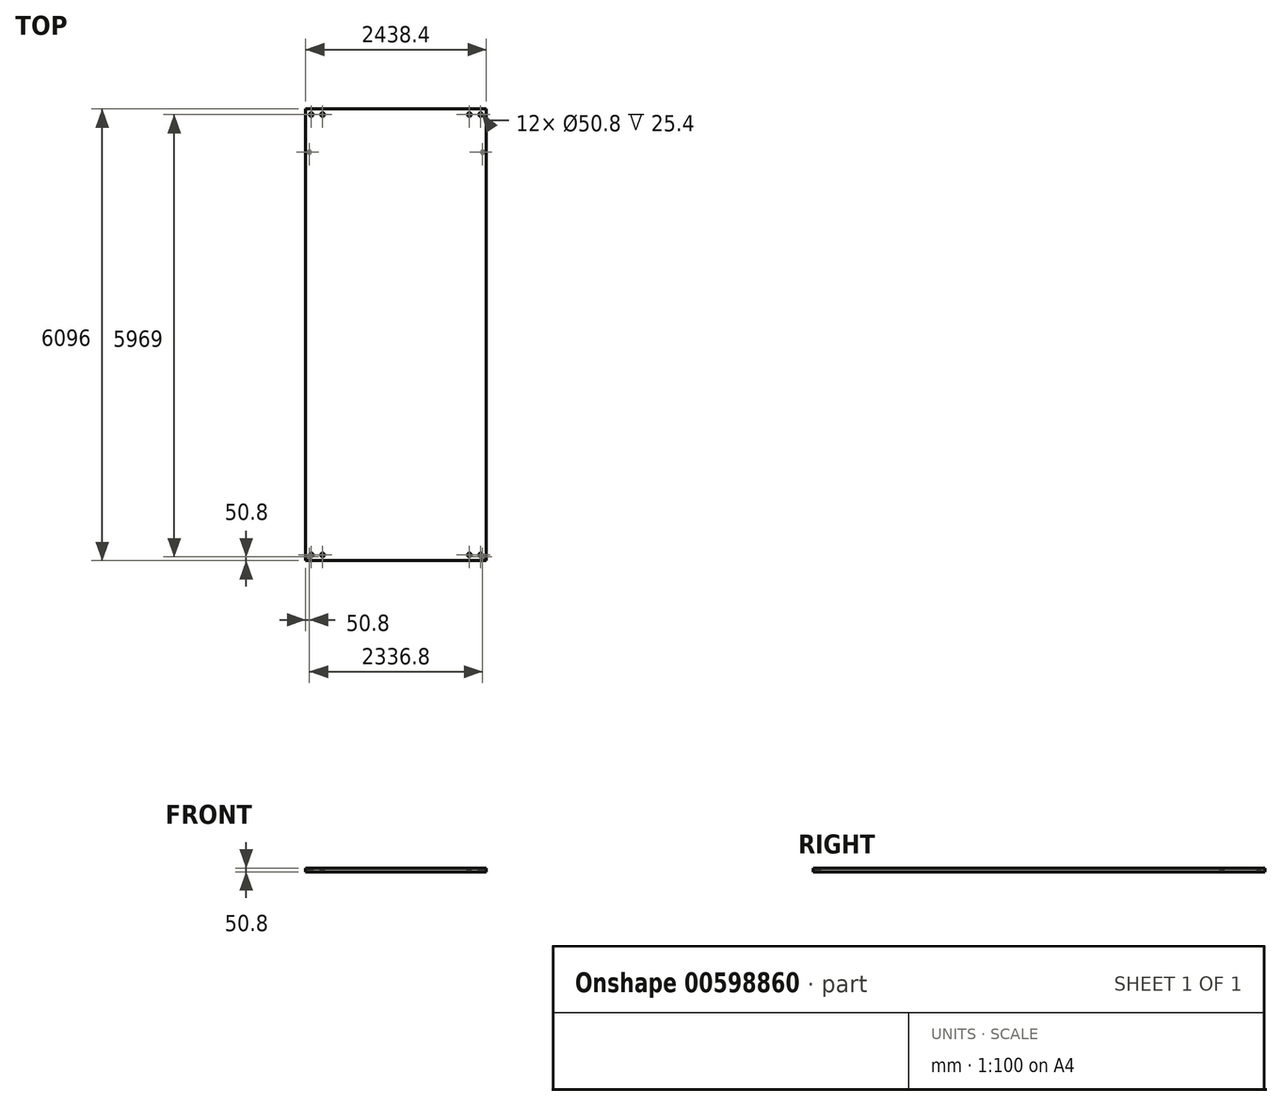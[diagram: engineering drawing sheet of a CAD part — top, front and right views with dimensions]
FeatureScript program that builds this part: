
annotation { "Feature Type Name" : "Feature", "Feature Type Description" : "" }
export const myFeature = defineFeature(function(context is Context, id is Id, definition is map)
    precondition{}
    {
        {
            var Q0;
            Q0=qCreatedBy(makeId("Top.planeOp"),FACE);
            var sketch = newSketch(context, id + "F0", { "sketchPlane" : qUnion([Q0])});
            skLineSegment(sketch, "E0.bottom", {"start": v(1219.2, 3048) * mm, "end": v(-1219.2, 3048) * mm});
            skLineSegment(sketch, "E0.top", {"start": v(1219.2, -3048) * mm, "end": v(-1219.2, -3048) * mm});
            skLineSegment(sketch, "E0.left", {"start": v(1219.2, 3048) * mm, "end": v(1219.2, -3048) * mm});
            skLineSegment(sketch, "E0.right", {"start": v(-1219.2, 3048) * mm, "end": v(-1219.2, -3048) * mm});
            skPoint(sketch, "E0.middle", {"position": v(0, 0) * mm});
            skSolve(sketch);
        }
        {
            var Q0;
            Q0=makeQuery(id+"F0.imprint","IMPRINT",FACE,{"disambiguationData":[TD([[makeQuery(id+"F0.imprint","IMPRINT",EDGE,{"derivedFrom":sQuery(id+"F0.wireOp",EDGE,"E0.bottom")}),1.0]])]});
            extrude(context, id + "F1", {"entities" : qUnion([Q0]), "depth" : 50.8 * mm, "offsetDistance" : 25.4 * mm});
        }
        {
            var Q0;
            Q0=makeQuery(id+"F1.opExtrude","CAP_FACE",FACE,{"disambiguationData":[OSD([sQuery(id+"F0.wireOp",EDGE,"E0.bottom"),sQuery(id+"F0.wireOp",EDGE,"E0.top"),sQuery(id+"F0.wireOp",EDGE,"E0.left"),sQuery(id+"F0.wireOp",EDGE,"E0.right")])],"isStart":false});
            var sketch = newSketch(context, id + "F2", { "sketchPlane" : qUnion([Q0])});
            skLineSegment(sketch, "E1.bottom", {"start": v(1219.2, -3048) * mm, "end": v(1143, -3048) * mm});
            skLineSegment(sketch, "E1.top", {"start": v(1219.2, -2971.8) * mm, "end": v(1143, -2971.8) * mm});
            skLineSegment(sketch, "E1.left", {"start": v(1219.2, -3048) * mm, "end": v(1219.2, -2971.8) * mm});
            skLineSegment(sketch, "E1.right", {"start": v(1143, -3048) * mm, "end": v(1143, -2971.8) * mm});
            skLineSegment(sketch, "E2.bottom", {"start": v(-1219.2, -3048) * mm, "end": v(-1143, -3048) * mm});
            skLineSegment(sketch, "E2.top", {"start": v(-1219.2, -2971.8) * mm, "end": v(-1143, -2971.8) * mm});
            skLineSegment(sketch, "E2.left", {"start": v(-1219.2, -3048) * mm, "end": v(-1219.2, -2971.8) * mm});
            skLineSegment(sketch, "E2.right", {"start": v(-1143, -3048) * mm, "end": v(-1143, -2971.8) * mm});
            skLineSegment(sketch, "E3.bottom", {"start": v(1219.2, 3048) * mm, "end": v(1143, 3048) * mm});
            skLineSegment(sketch, "E3.top", {"start": v(1219.2, 2971.8) * mm, "end": v(1143, 2971.8) * mm});
            skLineSegment(sketch, "E3.left", {"start": v(1219.2, 3048) * mm, "end": v(1219.2, 2971.8) * mm});
            skLineSegment(sketch, "E3.right", {"start": v(1143, 3048) * mm, "end": v(1143, 2971.8) * mm});
            skLineSegment(sketch, "E4.bottom", {"start": v(-1219.2, 3048) * mm, "end": v(-1143, 3048) * mm});
            skLineSegment(sketch, "E4.top", {"start": v(-1219.2, 2971.8) * mm, "end": v(-1143, 2971.8) * mm});
            skLineSegment(sketch, "E4.left", {"start": v(-1219.2, 3048) * mm, "end": v(-1219.2, 2971.8) * mm});
            skLineSegment(sketch, "E4.right", {"start": v(-1143, 3048) * mm, "end": v(-1143, 2971.8) * mm});
            skCircle(sketch, "E5", {"center": v(-1143, 2971.8) * mm, "radius": 25.4 * mm});
            skCircle(sketch, "E6", {"center": v(1143, 2971.8) * mm, "radius": 25.4 * mm});
            skCircle(sketch, "E7", {"center": v(1143, -2971.8) * mm, "radius": 25.4 * mm});
            skCircle(sketch, "E8", {"center": v(-1143, -2971.8) * mm, "radius": 25.4 * mm});
            skSolve(sketch);
        }
        {
            var Q0;
            {var subQ0=sQuery(id+"F2.wireOp",EDGE,"E3.right");var subQ1=sQuery(id+"F2.wireOp",EDGE,"E3.top");var subQ2=makeQuery(id+"F2.imprint","INTERSECT",VERTEX,{"derivedFrom":[subQ1,subQ0]});Q0=makeQuery(id+"F2.imprint","IMPRINT",FACE,{"disambiguationData":[TD([[makeQuery(id+"F2.imprint","IMPRINT",EDGE,{"disambiguationData":[TD([[subQ2,1.0]])],"derivedFrom":subQ1}),-1.0]])]});}
            var Q1;
            {var subQ0=sQuery(id+"F2.wireOp",EDGE,"E3.right");var subQ1=sQuery(id+"F2.wireOp",EDGE,"E3.top");var subQ2=makeQuery(id+"F2.imprint","INTERSECT",VERTEX,{"derivedFrom":[subQ1,subQ0]});Q1=makeQuery(id+"F2.imprint","IMPRINT",FACE,{"disambiguationData":[TD([[makeQuery(id+"F2.imprint","IMPRINT",EDGE,{"disambiguationData":[TD([[subQ2,1.0]])],"derivedFrom":subQ1}),1.0]])]});}
            var Q2;
            {var subQ0=sQuery(id+"F2.wireOp",EDGE,"E1.right");var subQ1=sQuery(id+"F2.wireOp",EDGE,"E1.top");var subQ2=makeQuery(id+"F2.imprint","INTERSECT",VERTEX,{"derivedFrom":[subQ1,subQ0]});Q2=makeQuery(id+"F2.imprint","IMPRINT",FACE,{"disambiguationData":[TD([[makeQuery(id+"F2.imprint","IMPRINT",EDGE,{"disambiguationData":[TD([[subQ2,1.0]])],"derivedFrom":subQ1}),1.0]])]});}
            var Q3;
            {var subQ0=sQuery(id+"F2.wireOp",EDGE,"E1.right");var subQ1=sQuery(id+"F2.wireOp",EDGE,"E1.top");var subQ2=makeQuery(id+"F2.imprint","INTERSECT",VERTEX,{"derivedFrom":[subQ1,subQ0]});Q3=makeQuery(id+"F2.imprint","IMPRINT",FACE,{"disambiguationData":[TD([[makeQuery(id+"F2.imprint","IMPRINT",EDGE,{"disambiguationData":[TD([[subQ2,1.0]])],"derivedFrom":subQ1}),-1.0]])]});}
            var Q4;
            {var subQ0=sQuery(id+"F2.wireOp",EDGE,"E2.right");var subQ1=sQuery(id+"F2.wireOp",EDGE,"E2.top");var subQ2=makeQuery(id+"F2.imprint","INTERSECT",VERTEX,{"derivedFrom":[subQ1,subQ0]});Q4=makeQuery(id+"F2.imprint","IMPRINT",FACE,{"disambiguationData":[TD([[makeQuery(id+"F2.imprint","IMPRINT",EDGE,{"disambiguationData":[TD([[subQ2,1.0]])],"derivedFrom":subQ1}),-1.0]])]});}
            var Q5;
            {var subQ0=sQuery(id+"F2.wireOp",EDGE,"E2.right");var subQ1=sQuery(id+"F2.wireOp",EDGE,"E2.top");var subQ2=makeQuery(id+"F2.imprint","INTERSECT",VERTEX,{"derivedFrom":[subQ1,subQ0]});Q5=makeQuery(id+"F2.imprint","IMPRINT",FACE,{"disambiguationData":[TD([[makeQuery(id+"F2.imprint","IMPRINT",EDGE,{"disambiguationData":[TD([[subQ2,1.0]])],"derivedFrom":subQ1}),1.0]])]});}
            var Q6;
            {var subQ0=sQuery(id+"F2.wireOp",EDGE,"E4.right");var subQ1=sQuery(id+"F2.wireOp",EDGE,"E4.top");var subQ2=makeQuery(id+"F2.imprint","INTERSECT",VERTEX,{"derivedFrom":[subQ1,subQ0]});Q6=makeQuery(id+"F2.imprint","IMPRINT",FACE,{"disambiguationData":[TD([[makeQuery(id+"F2.imprint","IMPRINT",EDGE,{"disambiguationData":[TD([[subQ2,1.0]])],"derivedFrom":subQ1}),1.0]])]});}
            var Q7;
            {var subQ0=sQuery(id+"F2.wireOp",EDGE,"E4.right");var subQ1=sQuery(id+"F2.wireOp",EDGE,"E4.top");var subQ2=makeQuery(id+"F2.imprint","INTERSECT",VERTEX,{"derivedFrom":[subQ1,subQ0]});Q7=makeQuery(id+"F2.imprint","IMPRINT",FACE,{"disambiguationData":[TD([[makeQuery(id+"F2.imprint","IMPRINT",EDGE,{"disambiguationData":[TD([[subQ2,1.0]])],"derivedFrom":subQ1}),-1.0]])]});}
            extrude(context, id + "F3", {"entities" : qUnion([Q0, Q1, Q2, Q3, Q4, Q5, Q6, Q7]), "operationType" : NewBodyOperationType.REMOVE, "oppositeDirection" : true, "depth" : 25.4 * mm, "offsetDistance" : 25.4 * mm});
        }
        {
            var Q0;
            Q0=makeQuery(id+"F1.opExtrude","CAP_FACE",FACE,{"disambiguationData":[OSD([sQuery(id+"F0.wireOp",EDGE,"E0.bottom"),sQuery(id+"F0.wireOp",EDGE,"E0.top"),sQuery(id+"F0.wireOp",EDGE,"E0.left"),sQuery(id+"F0.wireOp",EDGE,"E0.right")])],"isStart":false});
            var sketch = newSketch(context, id + "F4", { "sketchPlane" : qUnion([Q0])});
            skLineSegment(sketch, "E9.bottom", {"start": v(-1219.2, 3048) * mm, "end": v(-990.6, 3048) * mm});
            skLineSegment(sketch, "E9.top", {"start": v(-1219.2, 2971.8) * mm, "end": v(-990.6, 2971.8) * mm});
            skLineSegment(sketch, "E9.left", {"start": v(-1219.2, 3048) * mm, "end": v(-1219.2, 2971.8) * mm});
            skLineSegment(sketch, "E9.right", {"start": v(-990.6, 3048) * mm, "end": v(-990.6, 2971.8) * mm});
            skCircle(sketch, "E10", {"center": v(-990.6, 2971.8) * mm, "radius": 25.4 * mm});
            skLineSegment(sketch, "E11.bottom", {"start": v(1219.2, 3048) * mm, "end": v(990.6, 3048) * mm});
            skLineSegment(sketch, "E11.top", {"start": v(1219.2, 2971.8) * mm, "end": v(990.6, 2971.8) * mm});
            skLineSegment(sketch, "E11.left", {"start": v(1219.2, 3048) * mm, "end": v(1219.2, 2971.8) * mm});
            skLineSegment(sketch, "E11.right", {"start": v(990.6, 3048) * mm, "end": v(990.6, 2971.8) * mm});
            skCircle(sketch, "E12", {"center": v(990.6, 2971.8) * mm, "radius": 25.4 * mm});
            skLineSegment(sketch, "E13.bottom", {"start": v(-1219.2, -3048) * mm, "end": v(-990.6, -3048) * mm});
            skLineSegment(sketch, "E13.top", {"start": v(-1219.2, -2971.8) * mm, "end": v(-990.6, -2971.8) * mm});
            skLineSegment(sketch, "E13.left", {"start": v(-1219.2, -3048) * mm, "end": v(-1219.2, -2971.8) * mm});
            skLineSegment(sketch, "E13.right", {"start": v(-990.6, -3048) * mm, "end": v(-990.6, -2971.8) * mm});
            skLineSegment(sketch, "E14.bottom", {"start": v(1219.2, -3048) * mm, "end": v(990.6, -3048) * mm});
            skLineSegment(sketch, "E14.top", {"start": v(1219.2, -2971.8) * mm, "end": v(990.6, -2971.8) * mm});
            skLineSegment(sketch, "E14.left", {"start": v(1219.2, -3048) * mm, "end": v(1219.2, -2971.8) * mm});
            skLineSegment(sketch, "E14.right", {"start": v(990.6, -3048) * mm, "end": v(990.6, -2971.8) * mm});
            skCircle(sketch, "E15", {"center": v(-990.6, -2971.8) * mm, "radius": 25.4 * mm});
            skCircle(sketch, "E16", {"center": v(990.6, -2971.8) * mm, "radius": 25.4 * mm});
            skSolve(sketch);
        }
        {
            var Q0;
            {var subQ0=sQuery(id+"F4.wireOp",EDGE,"E14.right");var subQ1=sQuery(id+"F4.wireOp",EDGE,"E14.top");var subQ2=makeQuery(id+"F4.imprint","INTERSECT",VERTEX,{"derivedFrom":[subQ1,subQ0]});Q0=makeQuery(id+"F4.imprint","IMPRINT",FACE,{"disambiguationData":[TD([[makeQuery(id+"F4.imprint","IMPRINT",EDGE,{"disambiguationData":[TD([[subQ2,1.0]])],"derivedFrom":subQ1}),-1.0]])]});}
            var Q1;
            {var subQ0=sQuery(id+"F4.wireOp",EDGE,"E14.right");var subQ1=sQuery(id+"F4.wireOp",EDGE,"E14.top");var subQ2=makeQuery(id+"F4.imprint","INTERSECT",VERTEX,{"derivedFrom":[subQ1,subQ0]});Q1=makeQuery(id+"F4.imprint","IMPRINT",FACE,{"disambiguationData":[TD([[makeQuery(id+"F4.imprint","IMPRINT",EDGE,{"disambiguationData":[TD([[subQ2,1.0]])],"derivedFrom":subQ1}),1.0]])]});}
            var Q2;
            {var subQ0=sQuery(id+"F4.wireOp",EDGE,"E13.right");var subQ1=sQuery(id+"F4.wireOp",EDGE,"E13.top");var subQ2=makeQuery(id+"F4.imprint","INTERSECT",VERTEX,{"derivedFrom":[subQ1,subQ0]});Q2=makeQuery(id+"F4.imprint","IMPRINT",FACE,{"disambiguationData":[TD([[makeQuery(id+"F4.imprint","IMPRINT",EDGE,{"disambiguationData":[TD([[subQ2,1.0]])],"derivedFrom":subQ1}),-1.0]])]});}
            var Q3;
            {var subQ0=sQuery(id+"F4.wireOp",EDGE,"E13.right");var subQ1=sQuery(id+"F4.wireOp",EDGE,"E13.top");var subQ2=makeQuery(id+"F4.imprint","INTERSECT",VERTEX,{"derivedFrom":[subQ1,subQ0]});Q3=makeQuery(id+"F4.imprint","IMPRINT",FACE,{"disambiguationData":[TD([[makeQuery(id+"F4.imprint","IMPRINT",EDGE,{"disambiguationData":[TD([[subQ2,1.0]])],"derivedFrom":subQ1}),1.0]])]});}
            var Q4;
            {var subQ0=sQuery(id+"F4.wireOp",EDGE,"E11.right");var subQ1=sQuery(id+"F4.wireOp",EDGE,"E11.top");var subQ2=makeQuery(id+"F4.imprint","INTERSECT",VERTEX,{"derivedFrom":[subQ1,subQ0]});Q4=makeQuery(id+"F4.imprint","IMPRINT",FACE,{"disambiguationData":[TD([[makeQuery(id+"F4.imprint","IMPRINT",EDGE,{"disambiguationData":[TD([[subQ2,1.0]])],"derivedFrom":subQ1}),-1.0]])]});}
            var Q5;
            {var subQ0=sQuery(id+"F4.wireOp",EDGE,"E11.right");var subQ1=sQuery(id+"F4.wireOp",EDGE,"E11.top");var subQ2=makeQuery(id+"F4.imprint","INTERSECT",VERTEX,{"derivedFrom":[subQ1,subQ0]});Q5=makeQuery(id+"F4.imprint","IMPRINT",FACE,{"disambiguationData":[TD([[makeQuery(id+"F4.imprint","IMPRINT",EDGE,{"disambiguationData":[TD([[subQ2,1.0]])],"derivedFrom":subQ1}),1.0]])]});}
            var Q6;
            {var subQ0=sQuery(id+"F4.wireOp",EDGE,"E9.right");var subQ1=sQuery(id+"F4.wireOp",EDGE,"E9.top");var subQ2=makeQuery(id+"F4.imprint","INTERSECT",VERTEX,{"derivedFrom":[subQ1,subQ0]});Q6=makeQuery(id+"F4.imprint","IMPRINT",FACE,{"disambiguationData":[TD([[makeQuery(id+"F4.imprint","IMPRINT",EDGE,{"disambiguationData":[TD([[subQ2,1.0]])],"derivedFrom":subQ1}),1.0]])]});}
            var Q7;
            {var subQ0=sQuery(id+"F4.wireOp",EDGE,"E9.right");var subQ1=sQuery(id+"F4.wireOp",EDGE,"E9.top");var subQ2=makeQuery(id+"F4.imprint","INTERSECT",VERTEX,{"derivedFrom":[subQ1,subQ0]});Q7=makeQuery(id+"F4.imprint","IMPRINT",FACE,{"disambiguationData":[TD([[makeQuery(id+"F4.imprint","IMPRINT",EDGE,{"disambiguationData":[TD([[subQ2,1.0]])],"derivedFrom":subQ1}),-1.0]])]});}
            extrude(context, id + "F5", {"entities" : qUnion([Q0, Q1, Q2, Q3, Q4, Q5, Q6, Q7]), "operationType" : NewBodyOperationType.REMOVE, "oppositeDirection" : true, "depth" : 25.4 * mm, "offsetDistance" : 25.4 * mm});
        }
        {
            var Q0;
            Q0=makeQuery(id+"F1.opExtrude","CAP_FACE",FACE,{"disambiguationData":[OSD([sQuery(id+"F0.wireOp",EDGE,"E0.bottom"),sQuery(id+"F0.wireOp",EDGE,"E0.top"),sQuery(id+"F0.wireOp",EDGE,"E0.left"),sQuery(id+"F0.wireOp",EDGE,"E0.right")])],"isStart":true});
            var sketch = newSketch(context, id + "F6", { "sketchPlane" : qUnion([Q0])});
            skLineSegment(sketch, "E17", {"start": v(-1219.2, -3048) * mm, "end": v(-1219.2, -2514.6) * mm});
            skPoint(sketch, "E18", {"position": v(-1168.4, -2463.8) * mm});
            skCircle(sketch, "E19", {"center": v(-1168.4, -2463.8) * mm, "radius": 25.4 * mm});
            skPoint(sketch, "E20", {"position": v(1168.4, -2463.8) * mm});
            skCircle(sketch, "E21", {"center": v(1168.4, -2463.8) * mm, "radius": 25.4 * mm});
            skPoint(sketch, "E22", {"position": v(-1168.4, 2997.2) * mm});
            skPoint(sketch, "E23", {"position": v(1168.4, 2997.2) * mm});
            skCircle(sketch, "E24", {"center": v(-1168.4, 2997.2) * mm, "radius": 25.4 * mm});
            skCircle(sketch, "E25", {"center": v(1168.4, 2997.2) * mm, "radius": 25.4 * mm});
            skLineSegment(sketch, "E26", {"start": v(-1168.4, -2463.8) * mm, "end": v(1168.4, -2463.8) * mm});
            skSolve(sketch);
        }
        {
            var Q0;
            Q0=makeQuery(id+"F6.imprint","IMPRINT",FACE,{"disambiguationData":[TD([[makeQuery(id+"F6.imprint","IMPRINT",EDGE,{"derivedFrom":sQuery(id+"F6.wireOp",EDGE,"E19")}),1.0]])]});
            extrude(context, id + "F7", {"entities" : qUnion([Q0]), "operationType" : NewBodyOperationType.REMOVE, "oppositeDirection" : true, "depth" : 25.4 * mm, "offsetDistance" : 25.4 * mm});
        }
        {
            var Q0;
            Q0 = qSketchRegion(id + "F6", true);
            extrude(context, id + "F8", {"entities" : qUnion([Q0]), "operationType" : NewBodyOperationType.REMOVE, "oppositeDirection" : true, "depth" : 25.4 * mm, "offsetDistance" : 25.4 * mm});
        }
        {
            var Q0;
            Q0 = qSketchRegion(id + "F6", true);
            extrude(context, id + "F9", {"entities" : qUnion([Q0]), "operationType" : NewBodyOperationType.REMOVE, "oppositeDirection" : true, "depth" : 25.4 * mm, "offsetDistance" : 25.4 * mm});
        }
    });
